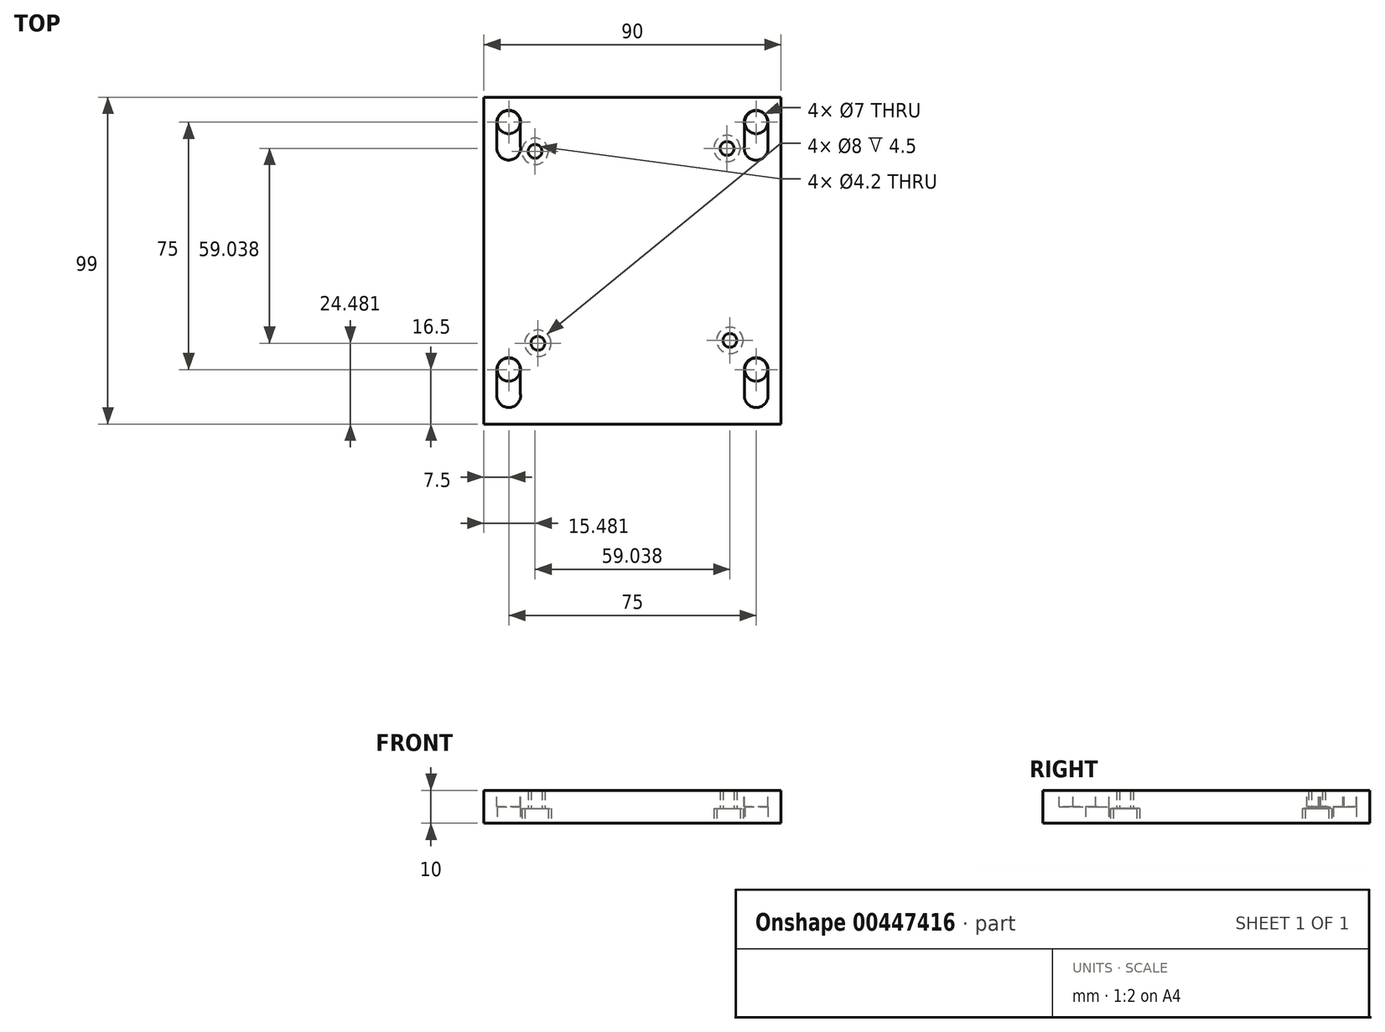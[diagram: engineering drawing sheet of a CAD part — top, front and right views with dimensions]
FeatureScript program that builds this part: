
annotation { "Feature Type Name" : "Feature", "Feature Type Description" : "" }
export const myFeature = defineFeature(function(context is Context, id is Id, definition is map)
    precondition{}
    {
        {
            var Q0;
            Q0=qCreatedBy(makeId("Top.planeOp"),FACE);
            var sketch = newSketch(context, id + "F0", { "sketchPlane" : qUnion([Q0])});
            skLineSegment(sketch, "E0.bottom", {"start": v(45, -45) * mm, "end": v(-45, -45) * mm});
            skLineSegment(sketch, "E0.top", {"start": v(45, 45) * mm, "end": v(-45, 45) * mm});
            skLineSegment(sketch, "E0.left", {"start": v(45, -45) * mm, "end": v(45, 45) * mm});
            skLineSegment(sketch, "E0.right", {"start": v(-45, -45) * mm, "end": v(-45, 45) * mm});
            skPoint(sketch, "E0.middle", {"position": v(0, 0) * mm});
            skCircle(sketch, "E1", {"center": v(-37.5, 37.5) * mm, "radius": 2.5 * mm});
            skCircle(sketch, "E2", {"center": v(37.5, 37.5) * mm, "radius": 2.5 * mm});
            skCircle(sketch, "E3", {"center": v(37.5, -37.5) * mm, "radius": 2.5 * mm});
            skCircle(sketch, "E4", {"center": v(-37.5, -37.5) * mm, "radius": 2.5 * mm});
            skLineSegment(sketch, "E5.bottom", {"start": v(-45, -45) * mm, "end": v(45, -45) * mm});
            skLineSegment(sketch, "E5.top", {"start": v(-45, -54) * mm, "end": v(45, -54) * mm});
            skLineSegment(sketch, "E5.left", {"start": v(-45, -45) * mm, "end": v(-45, -54) * mm});
            skLineSegment(sketch, "E5.right", {"start": v(45, -45) * mm, "end": v(45, -54) * mm});
            skSolve(sketch);
        }
        {
            var Q0;
            Q0 = qSketchRegion(id + "F0", true);
            extrude(context, id + "F1", {"entities" : qUnion([Q0]), "depth" : 10 * mm});
        }
        {
            var Q0;
            Q0=makeQuery(id+"F1.opExtrude","CAP_FACE",FACE,{"disambiguationData":[OSD([sQuery(id+"F0.wireOp",EDGE,"E0.bottom"),sQuery(id+"F0.wireOp",EDGE,"E0.top"),sQuery(id+"F0.wireOp",EDGE,"E0.left"),sQuery(id+"F0.wireOp",EDGE,"E0.right"),sQuery(id+"F0.wireOp",EDGE,"E1"),sQuery(id+"F0.wireOp",EDGE,"E2"),sQuery(id+"F0.wireOp",EDGE,"E3"),sQuery(id+"F0.wireOp",EDGE,"E4")])],"isStart":false});
            var sketch = newSketch(context, id + "F2", { "sketchPlane" : qUnion([Q0])});
            skArc(sketch, "E6", {"start": v(-33.94, 36.96) * mm, "mid": v(-37.5, 41.1) * mm, "end": v(-41.06, 36.96) * mm});
            skArc(sketch, "E7", {"start": v(-41.06, 30.15) * mm, "mid": v(-37.5, 26) * mm, "end": v(-33.94, 30.15) * mm});
            skLineSegment(sketch, "E8", {"start": v(-33.94, 30.15) * mm, "end": v(-33.94, 36.96) * mm});
            skLineSegment(sketch, "E9", {"start": v(-41.06, 36.96) * mm, "end": v(-41.06, 30.15) * mm});
            skArc(sketch, "E10", {"start": v(41.06, 37.38) * mm, "mid": v(37.22, 41.04) * mm, "end": v(33.9, 36.9) * mm});
            skArc(sketch, "E11", {"start": v(33.9, 30.1) * mm, "mid": v(37.22, 25.97) * mm, "end": v(41.06, 29.63) * mm});
            skLineSegment(sketch, "E12", {"start": v(41.06, 29.49) * mm, "end": v(41.06, 37.38) * mm});
            skLineSegment(sketch, "E13", {"start": v(33.9, 36.9) * mm, "end": v(33.9, 30.1) * mm});
            skArc(sketch, "E14", {"start": v(-33.94, -38.04) * mm, "mid": v(-37.5, -33.9) * mm, "end": v(-41.06, -38.04) * mm});
            skArc(sketch, "E15", {"start": v(-41.06, -44.85) * mm, "mid": v(-37.5, -49) * mm, "end": v(-33.94, -44.85) * mm});
            skLineSegment(sketch, "E16", {"start": v(-33.94, -44.85) * mm, "end": v(-33.94, -38.04) * mm});
            skLineSegment(sketch, "E17", {"start": v(-41.06, -38.04) * mm, "end": v(-41.06, -44.85) * mm});
            skPoint(sketch, "E18", {"position": v(-35.47, -36.04) * mm});
            skPoint(sketch, "E19", {"position": v(37.5, -37.5) * mm});
            skArc(sketch, "E20", {"start": v(41.06, -38.04) * mm, "mid": v(37.5, -33.9) * mm, "end": v(33.94, -38.04) * mm});
            skArc(sketch, "E21", {"start": v(33.94, -44.85) * mm, "mid": v(37.5, -49) * mm, "end": v(41.06, -44.85) * mm});
            skLineSegment(sketch, "E22", {"start": v(41.06, -44.85) * mm, "end": v(41.06, -38.04) * mm});
            skLineSegment(sketch, "E23", {"start": v(33.94, -38.04) * mm, "end": v(33.94, -44.85) * mm});
            skPoint(sketch, "E24", {"position": v(-27.36, -56.65) * mm});
            skSolve(sketch);
        }
        {
            var Q0;
            Q0 = qSketchRegion(id + "F2", true);
            extrude(context, id + "F3", {"entities" : qUnion([Q0]), "operationType" : NewBodyOperationType.REMOVE, "oppositeDirection" : true, "depth" : 5 * mm});
        }
        {
            var Q0;
            Q0=makeQuery(id+"F1.opExtrude","CAP_FACE",FACE,{"disambiguationData":[OSD([sQuery(id+"F0.wireOp",EDGE,"E0.top"),sQuery(id+"F0.wireOp",EDGE,"E0.left"),sQuery(id+"F0.wireOp",EDGE,"E0.right"),sQuery(id+"F0.wireOp",EDGE,"E1"),sQuery(id+"F0.wireOp",EDGE,"E2"),sQuery(id+"F0.wireOp",EDGE,"E3"),sQuery(id+"F0.wireOp",EDGE,"E4"),sQuery(id+"F0.wireOp",EDGE,"E5.top"),sQuery(id+"F0.wireOp",EDGE,"E5.left"),sQuery(id+"F0.wireOp",EDGE,"E5.right")])],"isStart":true});
            var sketch = newSketch(context, id + "F4", { "sketchPlane" : qUnion([Q0])});
            skCircle(sketch, "E25", {"center": v(-37.5, 37.5) * mm, "radius": 3.5 * mm});
            skCircle(sketch, "E26.1.0", {"center": v(-37.5, -37.5) * mm, "radius": 3.5 * mm});
            skCircle(sketch, "E26.2.0", {"center": v(37.5, -37.5) * mm, "radius": 3.5 * mm});
            skCircle(sketch, "E26.3.0", {"center": v(37.5, 37.5) * mm, "radius": 3.5 * mm});
            skPoint(sketch, "E26.center", {"position": v(0, 0) * mm});
            skSolve(sketch);
        }
        {
            var Q0;
            Q0=makeQuery(id+"F4.imprint","IMPRINT",FACE,{"disambiguationData":[TD([[makeQuery(id+"F4.imprint","IMPRINT",EDGE,{"derivedFrom":sQuery(id+"F4.wireOp",EDGE,"E26.1.0")}),1.0]])]});
            var Q1;
            Q1=makeQuery(id+"F4.imprint","IMPRINT",FACE,{"disambiguationData":[TD([[makeQuery(id+"F4.imprint","IMPRINT",EDGE,{"derivedFrom":sQuery(id+"F4.wireOp",EDGE,"E25")}),1.0]])]});
            var Q2;
            Q2=makeQuery(id+"F4.imprint","IMPRINT",FACE,{"disambiguationData":[TD([[makeQuery(id+"F4.imprint","IMPRINT",EDGE,{"derivedFrom":sQuery(id+"F4.wireOp",EDGE,"E26.3.0")}),1.0]])]});
            var Q3;
            Q3=makeQuery(id+"F4.imprint","IMPRINT",FACE,{"disambiguationData":[TD([[makeQuery(id+"F4.imprint","IMPRINT",EDGE,{"derivedFrom":sQuery(id+"F4.wireOp",EDGE,"E26.2.0")}),1.0]])]});
            var Q4;
            Q4=sQuery(id+"F4.wireOp",EDGE,"E25");
            var Q5;
            Q5=sQuery(id+"F4.wireOp",EDGE,"E26.3.0");
            var Q6;
            Q6=sQuery(id+"F4.wireOp",EDGE,"E26.2.0");
            var Q7;
            Q7=sQuery(id+"F4.wireOp",EDGE,"E26.1.0");
            extrude(context, id + "F5", {"entities" : qUnion([Q0, Q1, Q2, Q3]), "operationType" : NewBodyOperationType.REMOVE, "surfaceEntities" : qUnion([Q4, Q5, Q6, Q7]), "oppositeDirection" : true, "depth" : 25 * mm});
        }
        {
            var Q0;
            Q0=makeQuery(id+"F1.opExtrude","CAP_FACE",FACE,{"disambiguationData":[OSD([sQuery(id+"F0.wireOp",EDGE,"E0.top"),sQuery(id+"F0.wireOp",EDGE,"E0.left"),sQuery(id+"F0.wireOp",EDGE,"E0.right"),sQuery(id+"F0.wireOp",EDGE,"E1"),sQuery(id+"F0.wireOp",EDGE,"E2"),sQuery(id+"F0.wireOp",EDGE,"E3"),sQuery(id+"F0.wireOp",EDGE,"E4"),sQuery(id+"F0.wireOp",EDGE,"E5.top"),sQuery(id+"F0.wireOp",EDGE,"E5.left"),sQuery(id+"F0.wireOp",EDGE,"E5.right")])],"isStart":true});
            var sketch = newSketch(context, id + "F6", { "sketchPlane" : qUnion([Q0])});
            skCircle(sketch, "E27", {"center": v(-28.65, 29.52) * mm, "radius": 4 * mm});
            skCircle(sketch, "E28", {"center": v(-28.65, 29.52) * mm, "radius": 2.1 * mm});
            skCircle(sketch, "E29.1.0", {"center": v(-29.52, -28.65) * mm, "radius": 4 * mm});
            skCircle(sketch, "E29.1.1", {"center": v(-29.52, -28.65) * mm, "radius": 2.1 * mm});
            skCircle(sketch, "E29.2.0", {"center": v(28.65, -29.52) * mm, "radius": 4 * mm});
            skCircle(sketch, "E29.2.1", {"center": v(28.65, -29.52) * mm, "radius": 2.1 * mm});
            skCircle(sketch, "E29.3.0", {"center": v(29.52, 28.65) * mm, "radius": 4 * mm});
            skCircle(sketch, "E29.3.1", {"center": v(29.52, 28.65) * mm, "radius": 2.1 * mm});
            skPoint(sketch, "E29.center", {"position": v(0, 0) * mm});
            skSolve(sketch);
        }
        {
            var Q0;
            Q0=makeQuery(id+"F6.imprint","IMPRINT",FACE,{"disambiguationData":[TD([[makeQuery(id+"F6.imprint","IMPRINT",EDGE,{"derivedFrom":sQuery(id+"F6.wireOp",EDGE,"E29.1.0")}),1.0]])]});
            var Q1;
            Q1=makeQuery(id+"F6.imprint","IMPRINT",FACE,{"disambiguationData":[TD([[makeQuery(id+"F6.imprint","IMPRINT",EDGE,{"derivedFrom":sQuery(id+"F6.wireOp",EDGE,"E29.2.0")}),1.0]])]});
            var Q2;
            Q2=makeQuery(id+"F6.imprint","IMPRINT",FACE,{"disambiguationData":[TD([[makeQuery(id+"F6.imprint","IMPRINT",EDGE,{"derivedFrom":sQuery(id+"F6.wireOp",EDGE,"E27")}),1.0]])]});
            var Q3;
            Q3=makeQuery(id+"F6.imprint","IMPRINT",FACE,{"disambiguationData":[TD([[makeQuery(id+"F6.imprint","IMPRINT",EDGE,{"derivedFrom":sQuery(id+"F6.wireOp",EDGE,"E29.3.0")}),1.0]])]});
            extrude(context, id + "F7", {"entities" : qUnion([Q0, Q1, Q2, Q3]), "operationType" : NewBodyOperationType.REMOVE, "oppositeDirection" : true, "depth" : 4.5 * mm});
        }
        {
            var Q0;
            Q0=makeQuery(id+"F7.boolean.opBoolean","SPLIT",FACE,{"disambiguationData":[TD([makeQuery(id+"F7.opExtrude","SWEPT_FACE",FACE,{"disambiguationData":[OSD([sQuery(id+"F6.wireOp",EDGE,"E28")])]})])],"derivedFrom":makeQuery(id+"F1.opExtrude","CAP_FACE",FACE,{"disambiguationData":[OSD([sQuery(id+"F0.wireOp",EDGE,"E0.top"),sQuery(id+"F0.wireOp",EDGE,"E0.left"),sQuery(id+"F0.wireOp",EDGE,"E0.right"),sQuery(id+"F0.wireOp",EDGE,"E1"),sQuery(id+"F0.wireOp",EDGE,"E2"),sQuery(id+"F0.wireOp",EDGE,"E3"),sQuery(id+"F0.wireOp",EDGE,"E4"),sQuery(id+"F0.wireOp",EDGE,"E5.top"),sQuery(id+"F0.wireOp",EDGE,"E5.left"),sQuery(id+"F0.wireOp",EDGE,"E5.right")])],"isStart":true})});
            var Q1;
            Q1=makeQuery(id+"F7.boolean.opBoolean","SPLIT",FACE,{"disambiguationData":[TD([makeQuery(id+"F7.opExtrude","SWEPT_FACE",FACE,{"disambiguationData":[OSD([sQuery(id+"F6.wireOp",EDGE,"E29.3.1")])]})])],"derivedFrom":makeQuery(id+"F1.opExtrude","CAP_FACE",FACE,{"disambiguationData":[OSD([sQuery(id+"F0.wireOp",EDGE,"E0.top"),sQuery(id+"F0.wireOp",EDGE,"E0.left"),sQuery(id+"F0.wireOp",EDGE,"E0.right"),sQuery(id+"F0.wireOp",EDGE,"E1"),sQuery(id+"F0.wireOp",EDGE,"E2"),sQuery(id+"F0.wireOp",EDGE,"E3"),sQuery(id+"F0.wireOp",EDGE,"E4"),sQuery(id+"F0.wireOp",EDGE,"E5.top"),sQuery(id+"F0.wireOp",EDGE,"E5.left"),sQuery(id+"F0.wireOp",EDGE,"E5.right")])],"isStart":true})});
            var Q2;
            Q2=makeQuery(id+"F7.boolean.opBoolean","SPLIT",FACE,{"disambiguationData":[TD([makeQuery(id+"F7.opExtrude","SWEPT_FACE",FACE,{"disambiguationData":[OSD([sQuery(id+"F6.wireOp",EDGE,"E29.2.1")])]})])],"derivedFrom":makeQuery(id+"F1.opExtrude","CAP_FACE",FACE,{"disambiguationData":[OSD([sQuery(id+"F0.wireOp",EDGE,"E0.top"),sQuery(id+"F0.wireOp",EDGE,"E0.left"),sQuery(id+"F0.wireOp",EDGE,"E0.right"),sQuery(id+"F0.wireOp",EDGE,"E1"),sQuery(id+"F0.wireOp",EDGE,"E2"),sQuery(id+"F0.wireOp",EDGE,"E3"),sQuery(id+"F0.wireOp",EDGE,"E4"),sQuery(id+"F0.wireOp",EDGE,"E5.top"),sQuery(id+"F0.wireOp",EDGE,"E5.left"),sQuery(id+"F0.wireOp",EDGE,"E5.right")])],"isStart":true})});
            var Q3;
            Q3=makeQuery(id+"F7.boolean.opBoolean","SPLIT",FACE,{"disambiguationData":[TD([makeQuery(id+"F7.opExtrude","SWEPT_FACE",FACE,{"disambiguationData":[OSD([sQuery(id+"F6.wireOp",EDGE,"E29.1.1")])]})])],"derivedFrom":makeQuery(id+"F1.opExtrude","CAP_FACE",FACE,{"disambiguationData":[OSD([sQuery(id+"F0.wireOp",EDGE,"E0.top"),sQuery(id+"F0.wireOp",EDGE,"E0.left"),sQuery(id+"F0.wireOp",EDGE,"E0.right"),sQuery(id+"F0.wireOp",EDGE,"E1"),sQuery(id+"F0.wireOp",EDGE,"E2"),sQuery(id+"F0.wireOp",EDGE,"E3"),sQuery(id+"F0.wireOp",EDGE,"E4"),sQuery(id+"F0.wireOp",EDGE,"E5.top"),sQuery(id+"F0.wireOp",EDGE,"E5.left"),sQuery(id+"F0.wireOp",EDGE,"E5.right")])],"isStart":true})});
            extrude(context, id + "F8", {"entities" : qUnion([Q0, Q1, Q2, Q3]), "operationType" : NewBodyOperationType.REMOVE, "oppositeDirection" : true, "depth" : 25 * mm});
        }
    });
